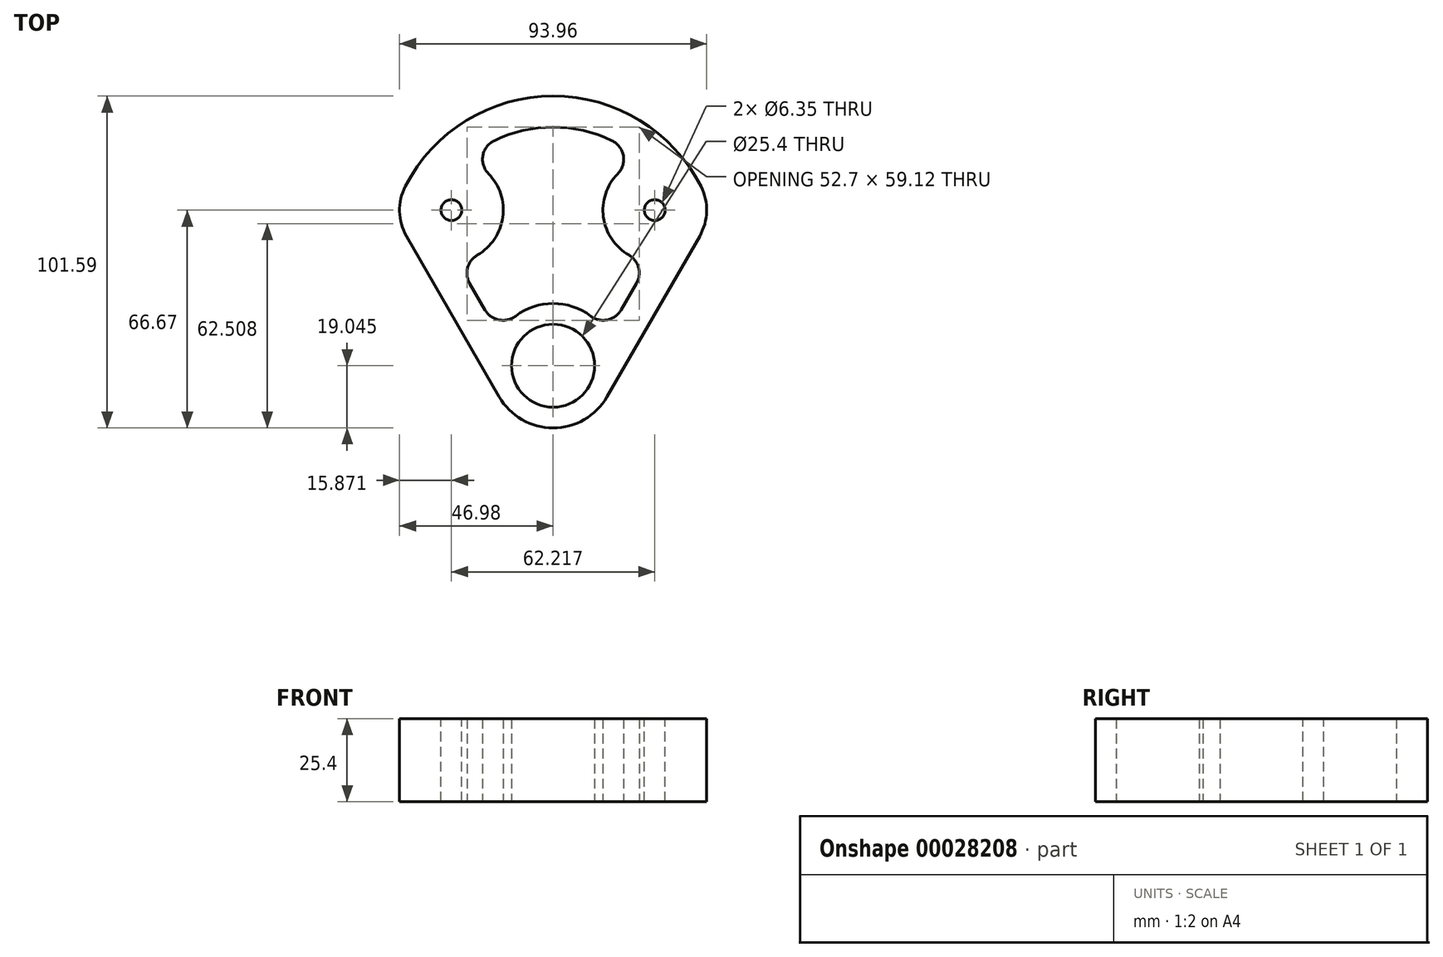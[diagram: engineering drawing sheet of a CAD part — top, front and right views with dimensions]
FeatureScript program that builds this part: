
annotation { "Feature Type Name" : "Feature", "Feature Type Description" : "" }
export const myFeature = defineFeature(function(context is Context, id is Id, definition is map)
    precondition{}
    {
        {
            var Q0;
            Q0=qCreatedBy(makeId("Top.planeOp"),FACE);
            var sketch = newSketch(context, id + "F0", { "sketchPlane" : qUnion([Q0])});
            skArc(sketch, "E0", {"start": v(45.25, 7.22) * mm, "mid": v(0, 34.93) * mm, "end": v(-45.25, 7.22) * mm});
            skArc(sketch, "E1", {"start": v(-45.25, 7.22) * mm, "mid": v(-46.98, -0.4) * mm, "end": v(-44.86, -7.93) * mm});
            skArc(sketch, "E2", {"start": v(19.77, 11.1) * mm, "mid": v(15.38, -2.16) * mm, "end": v(23.18, -13.75) * mm});
            skCircle(sketch, "E3", {"center": v(0, -47.62) * mm, "radius": 12.7 * mm});
            skArc(sketch, "E4", {"start": v(-16.5, -57.14) * mm, "mid": v(0, -66.67) * mm, "end": v(16.5, -57.14) * mm});
            skLineSegment(sketch, "E5", {"start": v(-44.86, -7.93) * mm, "end": v(-16.5, -57.14) * mm});
            skLineSegment(sketch, "E6", {"start": v(44.86, -7.93) * mm, "end": v(16.5, -57.14) * mm});
            skLineSegment(sketch, "E7", {"start": v(-25.51, -22.43) * mm, "end": v(-20.84, -30.55) * mm});
            skLineSegment(sketch, "E8", {"start": v(20.84, -30.55) * mm, "end": v(25.51, -22.43) * mm});
            skArc(sketch, "E9.trimOffspring", {"start": v(18, 21.27) * mm, "mid": v(0, 25.4) * mm, "end": v(-18, 21.27) * mm});
            skArc(sketch, "E10.trimOffspring", {"start": v(-23.18, -13.75) * mm, "mid": v(-15.38, -2.16) * mm, "end": v(-19.77, 11.1) * mm});
            skArc(sketch, "E11.trimOffspring", {"start": v(44.86, -7.93) * mm, "mid": v(46.98, -0.4) * mm, "end": v(45.25, 7.22) * mm});
            skArc(sketch, "E12.trimOffspring", {"start": v(11.5, -32.44) * mm, "mid": v(0, -28.58) * mm, "end": v(-11.5, -32.44) * mm});
            skPoint(sketch, "E13.visualSharp", {"position": v(27, 15.34) * mm});
            skArc(sketch, "E13.filletArc", {"start": v(19.77, 11.1) * mm, "mid": v(21.49, 16.64) * mm, "end": v(18, 21.27) * mm});
            skPoint(sketch, "E14.visualSharp", {"position": v(-27, 15.34) * mm});
            skArc(sketch, "E14.filletArc", {"start": v(-18, 21.27) * mm, "mid": v(-21.49, 16.64) * mm, "end": v(-19.77, 11.1) * mm});
            skPoint(sketch, "E15.visualSharp", {"position": v(-29.35, -15.78) * mm});
            skArc(sketch, "E15.filletArc", {"start": v(-23.18, -13.75) * mm, "mid": v(-26.14, -17.6) * mm, "end": v(-25.51, -22.43) * mm});
            skPoint(sketch, "E16.visualSharp", {"position": v(29.35, -15.78) * mm});
            skArc(sketch, "E16.filletArc", {"start": v(25.51, -22.43) * mm, "mid": v(26.14, -17.6) * mm, "end": v(23.18, -13.75) * mm});
            skPoint(sketch, "E17.visualSharp", {"position": v(16.49, -38.09) * mm});
            skArc(sketch, "E17.filletArc", {"start": v(11.5, -32.44) * mm, "mid": v(16.6, -33.6) * mm, "end": v(20.84, -30.55) * mm});
            skPoint(sketch, "E18.visualSharp", {"position": v(-16.49, -38.09) * mm});
            skArc(sketch, "E18.filletArc", {"start": v(-20.84, -30.55) * mm, "mid": v(-16.6, -33.6) * mm, "end": v(-11.5, -32.44) * mm});
            skSolve(sketch);
        }
        {
            var Q0;
            Q0 = qSketchRegion(id + "F0", true);
            extrude(context, id + "F1", {"entities" : qUnion([Q0]), "depth" : 25.4 * mm});
        }
        {
            var Q0;
            Q0=makeQuery(id+"F1.opExtrude","CAP_FACE",FACE,{"disambiguationData":[OSD([sQuery(id+"F0.wireOp",EDGE,"E0"),sQuery(id+"F0.wireOp",EDGE,"E1"),sQuery(id+"F0.wireOp",EDGE,"E2"),sQuery(id+"F0.wireOp",EDGE,"E3"),sQuery(id+"F0.wireOp",EDGE,"E4"),sQuery(id+"F0.wireOp",EDGE,"E5"),sQuery(id+"F0.wireOp",EDGE,"E6"),sQuery(id+"F0.wireOp",EDGE,"E7"),sQuery(id+"F0.wireOp",EDGE,"E8"),sQuery(id+"F0.wireOp",EDGE,"E9.trimOffspring"),sQuery(id+"F0.wireOp",EDGE,"E10.trimOffspring"),sQuery(id+"F0.wireOp",EDGE,"E11.trimOffspring"),sQuery(id+"F0.wireOp",EDGE,"E12.trimOffspring"),sQuery(id+"F0.wireOp",EDGE,"E13.filletArc"),sQuery(id+"F0.wireOp",EDGE,"E14.filletArc"),sQuery(id+"F0.wireOp",EDGE,"E15.filletArc"),sQuery(id+"F0.wireOp",EDGE,"E16.filletArc"),sQuery(id+"F0.wireOp",EDGE,"E17.filletArc"),sQuery(id+"F0.wireOp",EDGE,"E18.filletArc")])],"isStart":false});
            var sketch = newSketch(context, id + "F2", { "sketchPlane" : qUnion([Q0])});
            skPoint(sketch, "E19", {"position": v(-31.1, 0) * mm});
            skPoint(sketch, "E20", {"position": v(31.1, 0) * mm});
            skSolve(sketch);
        }
        {
            var Q0;
            Q0=sQuery(id+"F2.wireOp",VERTEX,"E19");
            var Q1;
            Q1=sQuery(id+"F2.wireOp",VERTEX,"E20");
            var Q2;
            Q2=makeQuery(id+"F1.opExtrude","SWEPT_BODY",BODY,{"disambiguationData":[OSD([sQuery(id+"F0.wireOp",EDGE,"E0"),sQuery(id+"F0.wireOp",EDGE,"E1"),sQuery(id+"F0.wireOp",EDGE,"E2"),sQuery(id+"F0.wireOp",EDGE,"E3"),sQuery(id+"F0.wireOp",EDGE,"E4"),sQuery(id+"F0.wireOp",EDGE,"E5"),sQuery(id+"F0.wireOp",EDGE,"E6"),sQuery(id+"F0.wireOp",EDGE,"E7"),sQuery(id+"F0.wireOp",EDGE,"E8"),sQuery(id+"F0.wireOp",EDGE,"E9.trimOffspring"),sQuery(id+"F0.wireOp",EDGE,"E10.trimOffspring"),sQuery(id+"F0.wireOp",EDGE,"E11.trimOffspring"),sQuery(id+"F0.wireOp",EDGE,"E12.trimOffspring"),sQuery(id+"F0.wireOp",EDGE,"E13.filletArc"),sQuery(id+"F0.wireOp",EDGE,"E14.filletArc"),sQuery(id+"F0.wireOp",EDGE,"E15.filletArc"),sQuery(id+"F0.wireOp",EDGE,"E16.filletArc"),sQuery(id+"F0.wireOp",EDGE,"E17.filletArc"),sQuery(id+"F0.wireOp",EDGE,"E18.filletArc")])]});
            hole(context, id + "F3", {"style" : HoleStyle.SIMPLE, "holeDiameter" : 6.35 * mm, "endStyle" : HoleEndStyle.THROUGH, "locations" : qUnion([Q0, Q1]), "scope" : qUnion([Q2])});
        }
    });
